# Revit family: Soap_Dispenser-Grohe-Cosmopolitan-40535_Series
name_source: partatom
category: Specialty Equipment
revit_build: Autodesk Revit 2018 (Build: 20170223_1515(x64)
units: mm (PartAtom-declared; Revit-internal decimal feet)

## family parameters
Always vertical = No
Cut with Voids When Loaded = No
OmniClass Number = 23.40.20.21.34
OmniClass Title = Soap Holders, Dispensers
Part Type = Normal
Room Calculation Point = No
Round Connector Dimension = Use Diameter
Shared = Yes
Work Plane-Based = Yes

## types (5) — shared parameters
Assembly Code = E2020200
Default Elevation = 0"
Description = Cosmopolitan Soap Dispenser
Height = 2 15/16"
Length = 3"
Manufacturer = Grohe
Price = Prices may vary. Please consult Manufacturer Representative for most up-to-date price list.
Product Page URL = https://www.grohe.us
Revised Date = 04/12/2021
URL = https://www.grohe.us
Width = 1 3/4"

## per-type parameters (varying)
| type | Finish | Material |
| 40535A00 | Metal-Grohe-A00-Hard Graphite | Metal-Grohe-A00-Hard Graphite |
| 40535BE0 | Metal-Grohe-BE0-Polished Nickel | Metal-Grohe-BE0-Polished Nickel |
| 40535GN0 | Metal-Grohe-GN0-Brushed Cool Sunset | Metal-Grohe-GN0-Brushed Cool Sunset |
| 40535000 | Metal-Grohe-000-Chrome | Metal-Grohe-000-Chrome |
| 40535DC0 | Metal-Grohe-BE0-Polished Nickel | Metal-Grohe-BE0-Polished Nickel |

note: column(s) folded — value = type name in every type: Model

## geometry (parser evidence)
native form markers: Sweep x2
no freeform markers — native parametric forms only
